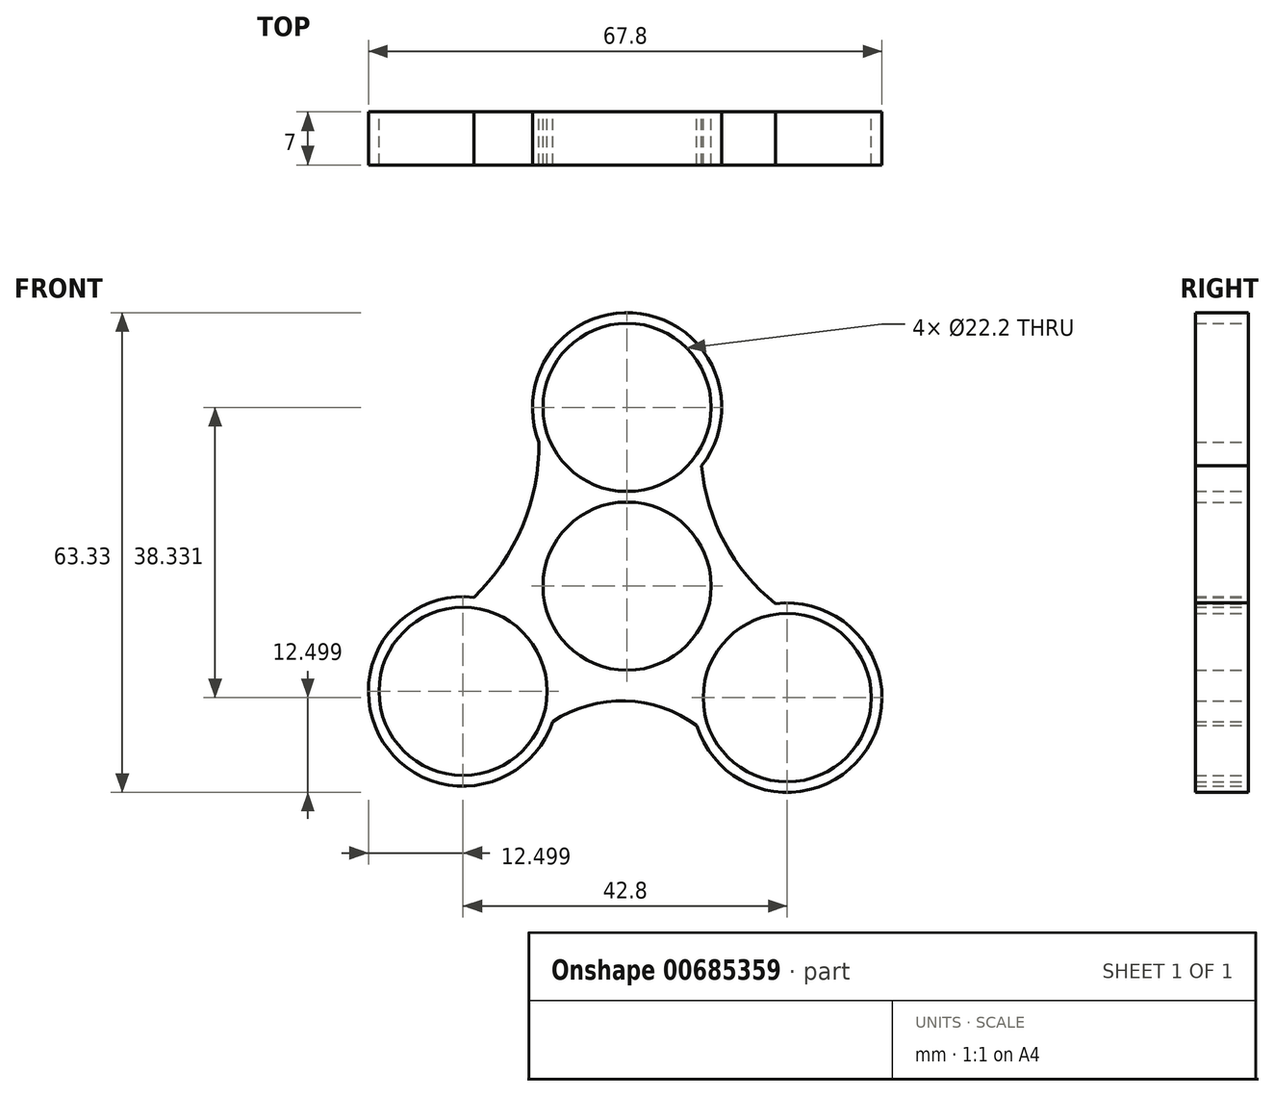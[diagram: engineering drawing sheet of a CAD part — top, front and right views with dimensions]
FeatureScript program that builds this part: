
annotation { "Feature Type Name" : "Feature", "Feature Type Description" : "" }
export const myFeature = defineFeature(function(context is Context, id is Id, definition is map)
    precondition{}
    {
        {
            var Q0;
            Q0=qCreatedBy(makeId("Front.planeOp"),FACE);
            var sketch = newSketch(context, id + "F0", { "sketchPlane" : qUnion([Q0])});
            skLineSegment(sketch, "E0", {"start": v(21.15, -3.63) * mm, "end": v(21.15, -3.48) * mm});
            skArc(sketch, "E1", {"start": v(-20.2, -1.48) * mm, "mid": v(-13.82, 7.9) * mm, "end": v(-11.63, 19.02) * mm});
            skArc(sketch, "E2", {"start": v(9.84, 15.9) * mm, "mid": v(12.85, 5.78) * mm, "end": v(19.6, -2.33) * mm});
            skArc(sketch, "E3", {"start": v(9.2, -18.4) * mm, "mid": v(-0.22, -15.16) * mm, "end": v(-9.8, -17.89) * mm});
            skArc(sketch, "E4", {"start": v(-20.2, -1.48) * mm, "mid": v(-32.2, -20.6) * mm, "end": v(-9.8, -17.89) * mm});
            skPoint(sketch, "E5.orphan", {"position": v(-21.65, -2.8) * mm});
            skArc(sketch, "E6", {"start": v(9.84, 15.9) * mm, "mid": v(1.8, 35.97) * mm, "end": v(-11.63, 19.02) * mm});
            skArc(sketch, "E7", {"start": v(9.2, -18.4) * mm, "mid": v(31.65, -21.52) * mm, "end": v(19.6, -2.33) * mm});
            skPoint(sketch, "E8.orphan", {"position": v(21.15, -3.48) * mm});
            skCircle(sketch, "E9", {"center": v(0, 0) * mm, "radius": 11.1 * mm});
            skCircle(sketch, "E10", {"center": v(0, 23.6) * mm, "radius": 11.1 * mm});
            skCircle(sketch, "E11", {"center": v(21.15, -14.73) * mm, "radius": 11.1 * mm});
            skCircle(sketch, "E12", {"center": v(-21.65, -13.9) * mm, "radius": 11.1 * mm});
            skPoint(sketch, "E13.orphan", {"position": v(-21.65, 8.3) * mm});
            skPoint(sketch, "E14.orphan", {"position": v(21.15, 0) * mm});
            skSolve(sketch);
        }
        {
            var Q0;
            Q0=makeQuery(id+"F0.imprint","IMPRINT",FACE,{"disambiguationData":[TD([[makeQuery(id+"F0.imprint","IMPRINT",EDGE,{"derivedFrom":sQuery(id+"F0.wireOp",EDGE,"E1")}),-1.0]])]});
            extrude(context, id + "F1", {"entities" : qUnion([Q0]), "depth" : 7 * mm, "offsetDistance" : 25 * mm});
        }
    });
